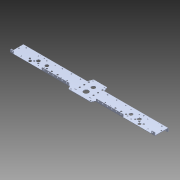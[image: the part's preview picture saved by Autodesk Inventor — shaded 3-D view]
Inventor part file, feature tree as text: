
AUTODESK INVENTOR PART (.ipt)
format: ipt  version: 2015 SP1 (Build 190203100, 203)  size: 504,320 bytes
history: native  units: in
note: dims shown in document units (in); Inventor stores cm internally (conversion verified against a paired STEP export)
features: reference x4, projected_geometry x3, other x2, extrude x2, sketch x2, chamfer x1, imported_body x1
ambient origin geometry x8: Origin, YZ Plane, XZ Plane, XY Plane, X Axis, Y Axis, Z Axis, Center Point
bodies: Body1 (feature_tree)
feature tree (15):
  other  "Cut-Extrude15"
  other  "AM14U2 Inside Sheet1"
  extrude  "Extrusion1"  Depth=6.25in
  extrude  "Extrusion2"  Depth=0.75in
  chamfer  "Chamfer1"  Distance=1.0in
  imported_body  "Base1"
  sketch  "Sketch1"  dims[d0=0.75in d1=6.25in]
  projected_geometry  "Projected Loop1"
  projected_geometry  "Projected Loop2"
  sketch  "Sketch2"  dims[d2=6.25in d3=0.75in d4=1.0in d5=0.0in d6=0.625in d7=0.625in d8=1.0in d9=0.0in d12=0.125in d13=0.125in d14=45.0deg]
  projected_geometry  "Projected Loop3"
  reference  "Reference1"
  reference  "Reference2"
  reference  "Reference3"
  reference  "Reference4"
